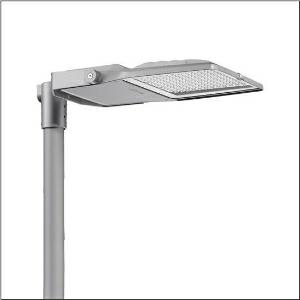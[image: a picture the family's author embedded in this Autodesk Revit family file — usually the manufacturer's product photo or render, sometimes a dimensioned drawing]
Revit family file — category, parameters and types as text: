
# Revit family: floodlight_fl_21_iq_midi___pl61_5xa7781f4c3a_8dc1
name_source: partatom
category: Lighting Fixtures
units: mm (PartAtom-declared; Revit-internal decimal feet)

## family parameters
Cut with Voids When Loaded = No
Host = Face
Light Source = No
Part Type = Normal
Room Calculation Point = No
Round Connector Dimension = Use Diameter
Shared = No

## types (1)
- --- (1 x LED, 36650 lm, 270.2 W, 4000K)
    Apparent Load = 270 VA
    CIE Flux Codes = 33 65 98 100 100
    Color Rendering = 70
    Color Temperature = 4000K
    Default Elevation = 1800 mm
    Description = Floodlight FL 21 iQ midi, floodlight, primary light control with lens, of PMMA, primary optical cover: protective disc, of toughened safety glass, transparent, light distribution: PL61, light emission: direct distribution, installation type: surface-mounted, LED, High Power LED, rated luminous flux: 36.650lm, luminous efficacy: 136lm/W, light colour: 740, colour temperature: 4000K, control gear: iQ Comfort/DALI, control: optimised constant luminous flux control (CLO 2.0), Desk-Remote (wireless, voltage-free reading and setting of iQ features in the workshop via application-optimized NFC function/RFID function), Light-Fading, Smart-Wire, Night-Set, Lumen-Switch, Temp-Guard, Auto-Match, with terminal, 6-pole, mains connection: 220..240V, AC, 50/60Hz, start of lifetime: 270W, end of service life: 287W, reduction: 118W, luminaire housing, of diecast aluminium, powder-coated, Siteco® metallic grey (DB 702S), corrosivity category C5 mid according to DIN EN ISO 12944, suitable for swimming pools, chlorine-resistant, sealing non-destructively replaceable, please order mast flange separately, mast bracket, of steel, galvanised, powder-coated, Siteco® metallic grey (DB 702S), protection rating (complete): IP66, insulation class (complete): insulation class II (safety insulation), certification: CE, ENEC, VDE, protection symbol: D, impact resistance: IK08, permissible operating ambient temperature: -40..+40°C, permissible operating ambient temperature for outdoor applications: -40..+50°C, standard: DIN EN 12944, LABS conformity tested according to VDMA 24364:2018-05, packaging unit: 1 piece

Light Distribution: PL61
    Height = 76 mm
    Lamp = 1 x LED
    Lamp Light Flux = 36650 lm
    Lamp Power = 270.2 W
    Lamp count = 1
    Length = 657 mm
    Luminous efficacy = 136 lm/W
    Manufacturer = Siteco
    ModVariant = No
    Model = 5XA7781F4C3A
    Number of Poles = 1
    OnlyDefault = Yes
    Power Factor = 1
    Product Name = Floodlight FL 21 iQ midi | PL61
    Product group = floodlight | pylon annexe
    ProductGroupID = 6200
    Protection Class = Protection class II
    Protection Degree = IP 66
    RLX_Detail_Level = 1
    RLX_Emergency_Light_Flux = 0 lm
    RLX_Emergency_Type = 0
    RLX_Emergency_Type_DB = No
    RlxData = <blob elided: 154085 chars, md5=c8b02632>
    Socket = socket
    Standby Power = 0 W
    System Light Flux = 36650 lm
    System Power = 270 W
    Type Comments = factory setting: luminous flux: 100 % | dim-lin: 254 | 620 mA
    Type Image = l_1007123.jpg
    URL = http://relux.com
    VarID = @adj_108412
    Voltage = 0 V
    Weight = 0.00 kg
    Width = 442 mm

## geometry (parser evidence)
native form markers: Blend x4, Sweep x13
no freeform markers — native parametric forms only
